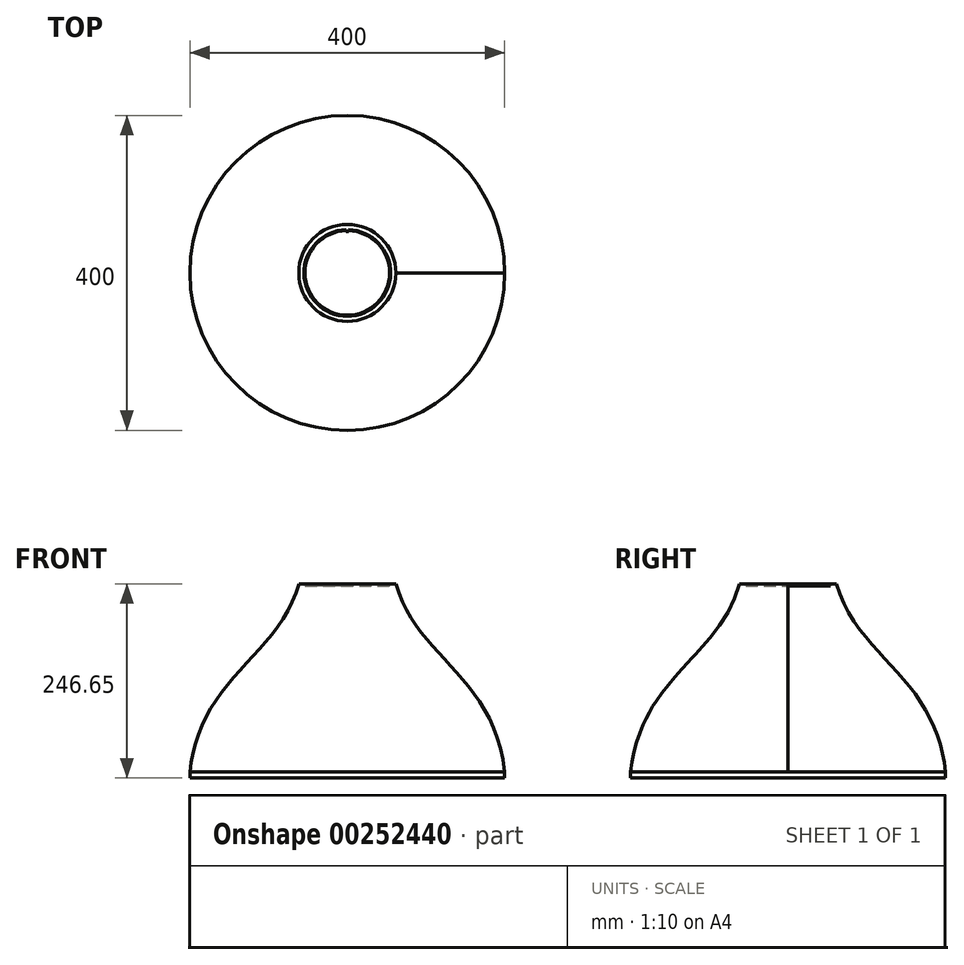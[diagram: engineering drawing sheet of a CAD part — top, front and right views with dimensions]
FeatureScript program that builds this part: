
annotation { "Feature Type Name" : "Feature", "Feature Type Description" : "" }
export const myFeature = defineFeature(function(context is Context, id is Id, definition is map)
    precondition{}
    {
        {
            var Q0;
            Q0=qCreatedBy(makeId("Front.planeOp"),FACE);
            var sketch = newSketch(context, id + "F0", { "sketchPlane" : qUnion([Q0])});
            skLineSegment(sketch, "E0", {"start": v(0, 0) * mm, "end": v(56, 0) * mm, "construction": true});
            skLineSegment(sketch, "E1", {"start": v(70, -212.57) * mm, "end": v(200, -212.57) * mm, "construction": true});
            skLineSegment(sketch, "E2", {"start": v(200, -212.57) * mm, "end": v(199, -212.57) * mm});
            skLineSegment(sketch, "E3", {"start": v(0, 0) * mm, "end": v(0, -240.08) * mm, "construction": true});
            skLineSegment(sketch, "E4", {"start": v(0, -215.13) * mm, "end": v(200, -215.13) * mm, "construction": true});
            skLineSegment(sketch, "E5", {"start": v(200, -215.13) * mm, "end": v(200, -207.19) * mm, "construction": true});
            skLineSegment(sketch, "E6", {"start": v(59, 3.96) * mm, "end": v(59, 31.52) * mm, "construction": true});
            skLineSegment(sketch, "E7", {"start": v(199, -212.57) * mm, "end": v(200, -212.57) * mm});
            skLineSegment(sketch, "E8", {"start": v(0, 28.82) * mm, "end": v(0, -215.13) * mm});
            skLineSegment(sketch, "E9", {"start": v(200, -215.13) * mm, "end": v(0, -215.13) * mm});
            skLineSegment(sketch, "E10", {"start": v(200, -212.57) * mm, "end": v(200, -215.13) * mm});
            skLineSegment(sketch, "E11", {"start": v(59, 31.52) * mm, "end": v(55, 31.52) * mm, "construction": true});
            skPoint(sketch, "E12", {"position": v(57, 31.52) * mm});
            skLineSegment(sketch, "E13", {"start": v(57, 31.52) * mm, "end": v(57, 26.28) * mm, "construction": true});
            skLineSegment(sketch, "E14.MirrorCS", {"start": v(55, 31.52) * mm, "end": v(53.7, 28.82) * mm});
            skLineSegment(sketch, "E15.trimOffspring", {"start": v(55, 31.52) * mm, "end": v(57, 31.52) * mm});
            skLineSegment(sketch, "E16", {"start": v(59, 31.52) * mm, "end": v(55, 31.52) * mm});
            skLineSegment(sketch, "E17", {"start": v(61.6, 31.52) * mm, "end": v(59, 31.52) * mm});
            skLineSegment(sketch, "E18", {"start": v(53.7, 28.82) * mm, "end": v(0, 28.82) * mm});
            skPoint(sketch, "E19.MirrorCS.end.orphan", {"position": v(53.7, 28.82) * mm});
            skLineSegment(sketch, "E20", {"start": v(56, 0) * mm, "end": v(56, 31.52) * mm, "construction": true});
            skFitSpline(sketch, "E21", {"points": [v(61.6, 31.52) * mm, v(200, -207.19) * mm], "startDerivative": vector(78.15, -280.93) * mm, "endDerivative": vector(43.32, -369.92) * mm});
            skLineSegment(sketch, "E22", {"start": v(200, -207.19) * mm, "end": v(200, -212.57) * mm});
            skSolve(sketch);
        }
        {
            var Q0;
            Q0=qCreatedBy(makeId("Front.planeOp"),FACE);
            var sketch = newSketch(context, id + "F1", { "sketchPlane" : qUnion([Q0])});
            skLineSegment(sketch, "E23", {"start": v(0, 75.24) * mm, "end": v(0, -198.52) * mm, "construction": true});
            skSolve(sketch);
        }
        {
            var Q0;
            Q0=makeQuery(id+"F0.imprint","IMPRINT",FACE,{"disambiguationData":[TD([[makeQuery(id+"F0.imprint","IMPRINT",EDGE,{"derivedFrom":sQuery(id+"F0.wireOp",EDGE,"E8")}),1.0]])]});
            var Q1;
            Q1=sQuery(id+"F1.wireOp",EDGE,"E23");
            revolve(context, id + "F2", {"entities" : qUnion([Q0]), "axis" : qUnion([Q1]), "revolveType" : RevolveType.FULL});
        }
        {
            var Q0;
            Q0=makeQuery(id+"F2.opRevolve","SWEPT_FACE",FACE,{"disambiguationData":[OSD([sQuery(id+"F0.wireOp",EDGE,"EVB5c4ay-B41Q-1dkQ-HLGU-uIXUuBqQrxcD"),sQuery(id+"F0.wireOp",EDGE,"2c460330-aff2-4c0a-b65b-7a3ef13a975f.trimOffspring"),sQuery(id+"F0.wireOp",EDGE,"E16"),sQuery(id+"F0.wireOp",EDGE,"E17")])]});
            var sketch = newSketch(context, id + "F3", { "sketchPlane" : qUnion([Q0])});
            skLineSegment(sketch, "E24", {"start": v(0, 52.82) * mm, "end": v(1.5, 52.82) * mm});
            skLineSegment(sketch, "E25", {"start": v(1.5, 52.82) * mm, "end": v(1.5, 55.32) * mm});
            skLineSegment(sketch, "E26", {"start": v(1.5, 55.32) * mm, "end": v(0, 55.32) * mm});
            skLineSegment(sketch, "E27", {"start": v(0, 55.32) * mm, "end": v(0, 52.82) * mm, "construction": true});
            skLineSegment(sketch, "E28.MirrorCS", {"start": v(-1.5, 55.32) * mm, "end": v(0, 55.32) * mm});
            skLineSegment(sketch, "E29.MirrorCS", {"start": v(-1.5, 52.82) * mm, "end": v(-1.5, 55.32) * mm});
            skLineSegment(sketch, "E30.MirrorCS", {"start": v(0, 52.82) * mm, "end": v(-1.5, 52.82) * mm});
            skSolve(sketch);
        }
        {
            var Q0;
            Q0 = qSketchRegion(id + "F3", true);
            var Q1;
            Q1=makeQuery(id+"F2.opRevolve","SWEPT_FACE",FACE,{"disambiguationData":[OSD([sQuery(id+"F0.wireOp",EDGE,"E18")])]});
            extrude(context, id + "F4", {"entities" : qUnion([Q0]), "operationType" : NewBodyOperationType.ADD, "endBound" : BoundingType.UP_TO_SURFACE, "oppositeDirection" : true, "endBoundEntityFace" : qUnion([Q1]), "depth" : 2.7 * mm});
        }
    });
